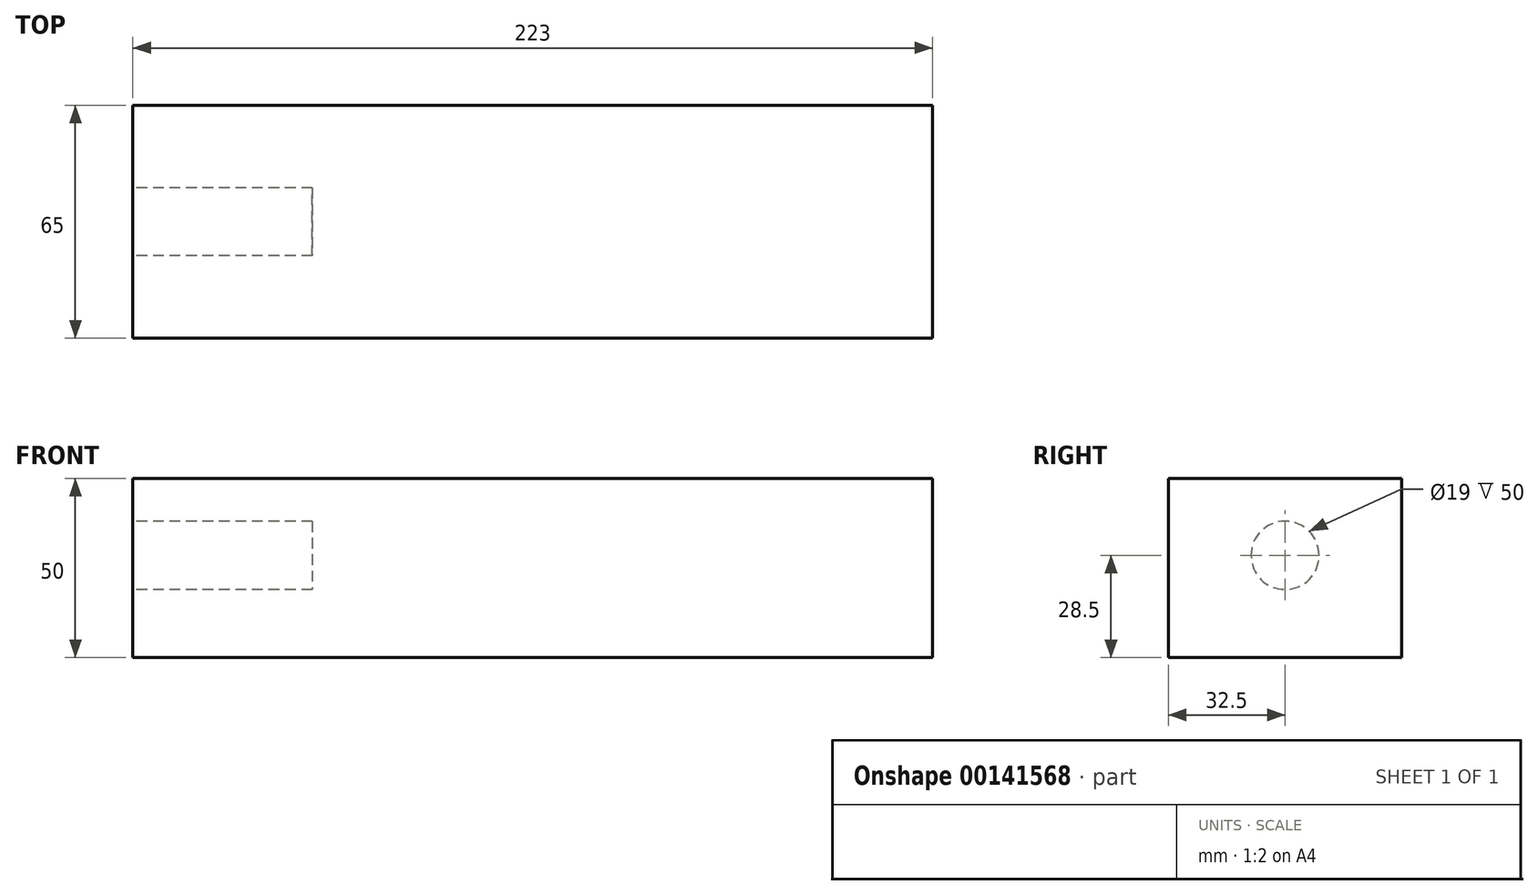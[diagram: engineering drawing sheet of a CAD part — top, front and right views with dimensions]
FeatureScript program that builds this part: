
annotation { "Feature Type Name" : "Feature", "Feature Type Description" : "" }
export const myFeature = defineFeature(function(context is Context, id is Id, definition is map)
    precondition{}
    {
        {
            var Q0;
            Q0=qCreatedBy(makeId("Right.planeOp"),FACE);
            var sketch = newSketch(context, id + "F0", { "sketchPlane" : qUnion([Q0])});
            skLineSegment(sketch, "E0.bottom", {"start": v(-32.5, 21.5) * mm, "end": v(32.5, 21.5) * mm});
            skLineSegment(sketch, "E0.top", {"start": v(-32.5, -28.5) * mm, "end": v(32.5, -28.5) * mm});
            skLineSegment(sketch, "E0.left", {"start": v(-32.5, 21.5) * mm, "end": v(-32.5, -28.5) * mm});
            skLineSegment(sketch, "E0.right", {"start": v(32.5, 21.5) * mm, "end": v(32.5, -28.5) * mm});
            skSolve(sketch);
        }
        {
            var Q0;
            Q0=makeQuery(id+"F0.imprint","IMPRINT",FACE,{"disambiguationData":[TD([[makeQuery(id+"F0.imprint","IMPRINT",EDGE,{"derivedFrom":sQuery(id+"F0.wireOp",EDGE,"E0.bottom")}),-1.0]])]});
            extrude(context, id + "F1", {"entities" : qUnion([Q0]), "depth" : 223 * mm});
        }
        {
            var Q0;
            Q0=makeQuery(id+"F1.opExtrude","CAP_FACE",FACE,{"disambiguationData":[OSD([sQuery(id+"F0.wireOp",EDGE,"E0.bottom"),sQuery(id+"F0.wireOp",EDGE,"E0.top"),sQuery(id+"F0.wireOp",EDGE,"E0.left"),sQuery(id+"F0.wireOp",EDGE,"E0.right")])],"isStart":true});
            var sketch = newSketch(context, id + "F2", { "sketchPlane" : qUnion([Q0])});
            skCircle(sketch, "E1", {"center": v(0, 0) * mm, "radius": 9.5 * mm});
            skSolve(sketch);
        }
        {
            var Q0;
            Q0=makeQuery(id+"F2.imprint","IMPRINT",FACE,{"disambiguationData":[TD([[makeQuery(id+"F2.imprint","IMPRINT",EDGE,{"derivedFrom":sQuery(id+"F2.wireOp",EDGE,"E1")}),1.0]])]});
            extrude(context, id + "F3", {"entities" : qUnion([Q0]), "operationType" : NewBodyOperationType.REMOVE, "oppositeDirection" : true, "depth" : 50 * mm});
        }
    });
